# Revit family: Plumbing-Sink-Sloan-Valve-EWF-43000
name_source: partatom
category: Plumbing Fixtures
units: mm (PartAtom-declared; Revit-internal decimal feet)

## family parameters
Cut with Voids When Loaded = No
Host = Face
OmniClass Number = 23.45.05.14.14
OmniClass Title = Sinks/Lavatories
Part Type = Normal
Room Calculation Point = No
Round Connector Dimension = Use Diameter
Shared = No

## types (2) — shared parameters
Apparent Load = 688 VA
Assembly Code = D2010400
CW Connection = Yes
CWFU = 1.5
Cold Water Connection Diameter = 1/2"
Current = 15 A
Default Elevation = 0"
Depth = 26"
Description = SloanStone® 3-Station Wall-Mounted Wash Fountain Sink.
Edition number = 1
Frequency = 60 Hz
HW Connection = Yes
HWFU = 1.5
Height = 39 1/2"
Hot Water Connection Diameter = 1/2"
Keynote = 10000
Manufacturer = Sloan Valve
Number of Poles = 3
Power Factor = 0.8
Product Material = Sloan - SloanStone - Pearl (PL)
Product data url = https://bimobject.com
Sanitary Drain Connection Diameter = 1 1/2"
URL = www.sloanvalve.com
Valve Pressure Drop = 0.0 Pa
Vent Connection = No
Voltage = 110 V
WFU = 2
Waste Connection = Yes
Water Flow = 0.5 GPM
Width = 36"

## per-type parameters (varying)
| type | z_FM |
| EWF-43000 | No |
| EWF-43000-FM | Yes |

note: column(s) folded — value = type name in every type: Model

## geometry (parser evidence)
native form markers: Sweep x4
no freeform markers — native parametric forms only
